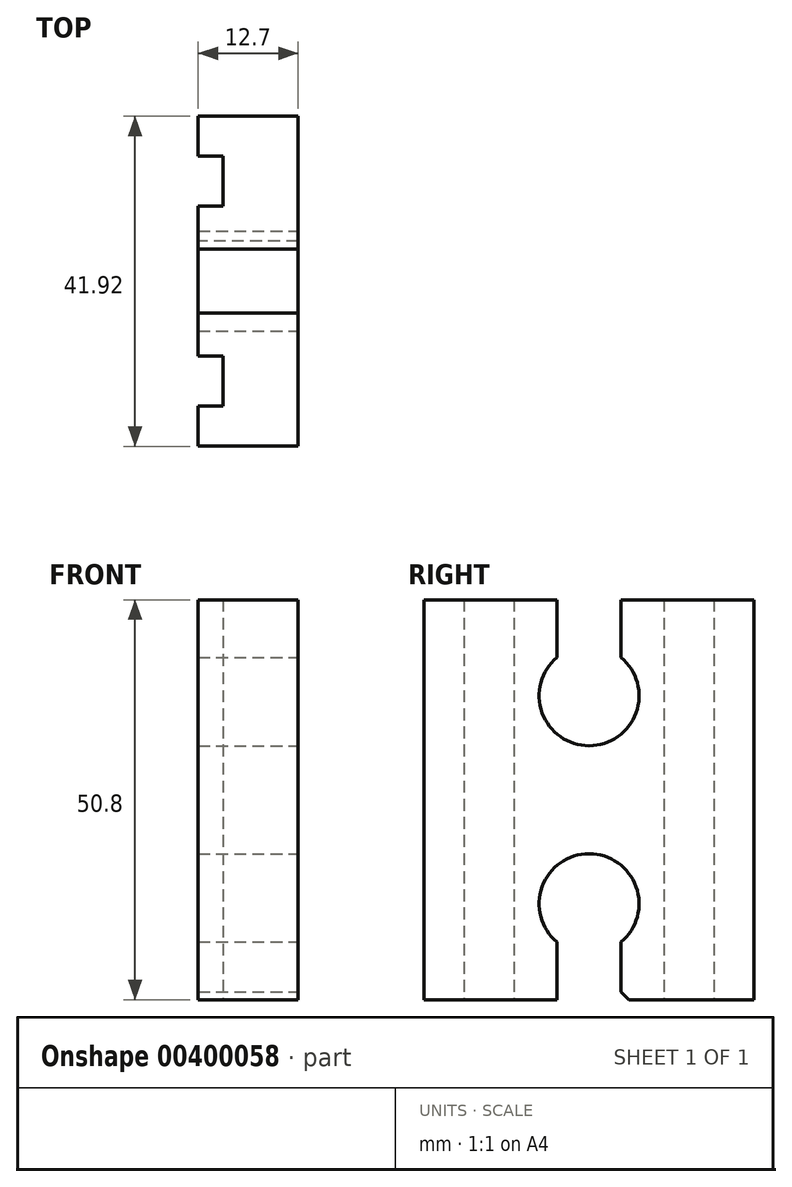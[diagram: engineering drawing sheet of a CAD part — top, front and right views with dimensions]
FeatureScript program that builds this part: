
annotation { "Feature Type Name" : "Feature", "Feature Type Description" : "" }
export const myFeature = defineFeature(function(context is Context, id is Id, definition is map)
    precondition{}
    {
        {
            var Q0;
            Q0=qCreatedBy(makeId("Top.planeOp"),FACE);
            var sketch = newSketch(context, id + "F0", { "sketchPlane" : qUnion([Q0])});
            skLineSegment(sketch, "E0", {"start": v(-12.7, -20.96) * mm, "end": v(-12.7, -15.88) * mm});
            skLineSegment(sketch, "E1", {"start": v(-12.7, -15.88) * mm, "end": v(-9.52, -15.88) * mm});
            skLineSegment(sketch, "E2", {"start": v(-9.52, -15.88) * mm, "end": v(-9.53, -9.53) * mm});
            skLineSegment(sketch, "E3", {"start": v(-9.53, -9.53) * mm, "end": v(-12.7, -9.53) * mm});
            skLineSegment(sketch, "E4", {"start": v(-12.7, -9.52) * mm, "end": v(-12.7, 9.52) * mm});
            skLineSegment(sketch, "E5", {"start": v(-12.7, 9.53) * mm, "end": v(-9.53, 9.53) * mm});
            skLineSegment(sketch, "E6", {"start": v(-9.53, 9.53) * mm, "end": v(-9.53, 15.88) * mm});
            skLineSegment(sketch, "E7", {"start": v(-9.53, 15.88) * mm, "end": v(-12.7, 15.88) * mm});
            skLineSegment(sketch, "E8", {"start": v(-12.7, 15.88) * mm, "end": v(-12.7, 20.96) * mm});
            skLineSegment(sketch, "E9", {"start": v(-12.7, 20.96) * mm, "end": v(0, 20.96) * mm});
            skLineSegment(sketch, "E10", {"start": v(0, 20.96) * mm, "end": v(0, -20.96) * mm});
            skLineSegment(sketch, "E11", {"start": v(0, -20.96) * mm, "end": v(-12.7, -20.96) * mm});
            skLineSegment(sketch, "E12", {"start": v(0, 0) * mm, "end": v(-24.05, 0) * mm, "construction": true});
            skSolve(sketch);
        }
        {
            var Q0;
            Q0 = qSketchRegion(id + "F0", true);
            extrude(context, id + "F1", {"entities" : qUnion([Q0]), "depth" : 50.8 * mm});
        }
        {
            var Q0;
            Q0=makeQuery(id+"F1.opExtrude","SWEPT_FACE",FACE,{"disambiguationData":[OSD([sQuery(id+"F0.wireOp",EDGE,"E10")])]});
            var sketch = newSketch(context, id + "F2", { "sketchPlane" : qUnion([Q0])});
            skLineSegment(sketch, "E13", {"start": v(0, 0) * mm, "end": v(0, 16.74) * mm, "construction": true});
            skLineSegment(sketch, "E14", {"start": v(-4.06, 0) * mm, "end": v(-4.06, 7.31) * mm});
            skLineSegment(sketch, "E15", {"start": v(4.06, 0) * mm, "end": v(4.06, 7.31) * mm});
            skArc(sketch, "E16", {"start": v(4.06, 7.31) * mm, "mid": v(0, 18.54) * mm, "end": v(-4.06, 7.31) * mm});
            skLineSegment(sketch, "E17", {"start": v(-4.06, 0) * mm, "end": v(4.06, 0) * mm});
            skSolve(sketch);
        }
        {
            var Q0;
            Q0 = qSketchRegion(id + "F2", true);
            extrude(context, id + "F3", {"entities" : qUnion([Q0]), "operationType" : NewBodyOperationType.REMOVE, "oppositeDirection" : true, "depth" : 25.4 * mm});
        }
        {
            var Q0;
            Q0=makeQuery(id+"F1.opExtrude","SWEPT_EDGE",EDGE,{"disambiguationData":[OSD([sQuery(id+"F0.wireOp",EDGE,"E10"),sQuery(id+"F0.wireOp",EDGE,"E11")])]});
            cPoint(context, id + "F4", {"entities" : qUnion([Q0]), "parameter" : 0.5});
        }
        {
            var Q0;
            {var subQ0=sQuery(id+"F0.wireOp",EDGE,"E2");var subQ1=sQuery(id+"F0.wireOp",EDGE,"E1");var subQ2=sQuery(id+"F0.wireOp",EDGE,"E3");var subQ3=sQuery(id+"F0.wireOp",EDGE,"E0");var subQ4=sQuery(id+"F0.wireOp",EDGE,"E4");var subQ5=sQuery(id+"F0.wireOp",EDGE,"E10");var subQ6=sQuery(id+"F0.wireOp",EDGE,"E11");Q0=makeQuery(id+"F3.boolean.opBoolean","SPLIT",FACE,{"disambiguationData":[TD([makeQuery(id+"F1.opExtrude","SWEPT_FACE",FACE,{"disambiguationData":[OSD([subQ3])]})])],"derivedFrom":makeQuery(id+"F1.opExtrude","CAP_FACE",FACE,{"disambiguationData":[OSD([subQ3,subQ1,subQ0,subQ2,subQ4,sQuery(id+"F0.wireOp",EDGE,"E5"),sQuery(id+"F0.wireOp",EDGE,"E6"),sQuery(id+"F0.wireOp",EDGE,"E7"),sQuery(id+"F0.wireOp",EDGE,"E8"),sQuery(id+"F0.wireOp",EDGE,"E9"),subQ5,subQ6])],"isStart":true})});}
            var Q1;
            Q1 = qCreatedBy(id + "F4" ,VERTEX);
            cPlane(context, id + "F5", {"entities" : qUnion([Q0, Q1]), "cplaneType" : CPlaneType.PLANE_POINT, "offset" : 25.4 * mm, "width" : 152.4 * mm, "height" : 152.4 * mm});
        }
        {
            var Q0;
            Q0=makeQuery(id+"F1.opExtrude","SWEPT_BODY",BODY,{"disambiguationData":[OSD([sQuery(id+"F0.wireOp",EDGE,"E0"),sQuery(id+"F0.wireOp",EDGE,"E1"),sQuery(id+"F0.wireOp",EDGE,"E2"),sQuery(id+"F0.wireOp",EDGE,"E3"),sQuery(id+"F0.wireOp",EDGE,"E4"),sQuery(id+"F0.wireOp",EDGE,"E5"),sQuery(id+"F0.wireOp",EDGE,"E6"),sQuery(id+"F0.wireOp",EDGE,"E7"),sQuery(id+"F0.wireOp",EDGE,"E8"),sQuery(id+"F0.wireOp",EDGE,"E9"),sQuery(id+"F0.wireOp",EDGE,"E10"),sQuery(id+"F0.wireOp",EDGE,"E11")])]});
            var Q1;
            Q1=qCreatedBy(id+"F5.planeOp",FACE);
            mirror(context, id + "F6", {"operationType" : NewBodyOperationType.INTERSECT, "entities" : qUnion([Q0]), "mirrorPlane" : qUnion([Q1])});
        }
        {
            var Q0;
            Q0=makeQuery(id+"F6.boolean.opBoolean","COPY",EDGE,{"derivedFrom":makeQuery(id+"F6.boolean.toolComplement.opBoolean","COPY",EDGE,{"derivedFrom":makeQuery(id+"F6.opPattern","COPY",EDGE,{"derivedFrom":makeQuery(id+"F3.boolean.opBoolean","COPY",EDGE,{"derivedFrom":makeQuery(id+"F3.opExtrude","SWEPT_EDGE",EDGE,{"disambiguationData":[OSD([sQuery(id+"F0.wireOp",EDGE,"E10"),sQuery(id+"F2.wireOp",EDGE,"E14"),sQuery(id+"F2.wireOp",EDGE,"E17")])]})}),"instanceName":"1"})})});
            var Q1;
            Q1=makeQuery(id+"F6.boolean.opBoolean","COPY",EDGE,{"derivedFrom":makeQuery(id+"F6.boolean.toolComplement.opBoolean","COPY",EDGE,{"derivedFrom":makeQuery(id+"F6.opPattern","COPY",EDGE,{"derivedFrom":makeQuery(id+"F3.boolean.opBoolean","COPY",EDGE,{"derivedFrom":makeQuery(id+"F3.opExtrude","SWEPT_EDGE",EDGE,{"disambiguationData":[OSD([sQuery(id+"F0.wireOp",EDGE,"E10"),sQuery(id+"F2.wireOp",EDGE,"E15"),sQuery(id+"F2.wireOp",EDGE,"E17")])]})}),"instanceName":"1"})})});
            var Q2;
            Q2=makeQuery(id+"F3.boolean.opBoolean","COPY",EDGE,{"derivedFrom":makeQuery(id+"F3.opExtrude","SWEPT_EDGE",EDGE,{"disambiguationData":[OSD([sQuery(id+"F0.wireOp",EDGE,"E10"),sQuery(id+"F2.wireOp",EDGE,"E15"),sQuery(id+"F2.wireOp",EDGE,"E17")])]})});
            var Q3;
            Q3=makeQuery(id+"F3.boolean.opBoolean","COPY",EDGE,{"derivedFrom":makeQuery(id+"F3.opExtrude","SWEPT_EDGE",EDGE,{"disambiguationData":[OSD([sQuery(id+"F0.wireOp",EDGE,"E10"),sQuery(id+"F2.wireOp",EDGE,"E14"),sQuery(id+"F2.wireOp",EDGE,"E17")])]})});
            chamfer(context, id + "F7", {"entities" : qUnion([Q0, Q1, Q2, Q3]), "width" : 1.02 * mm, "tangentPropagation" : true});
        }
    });
